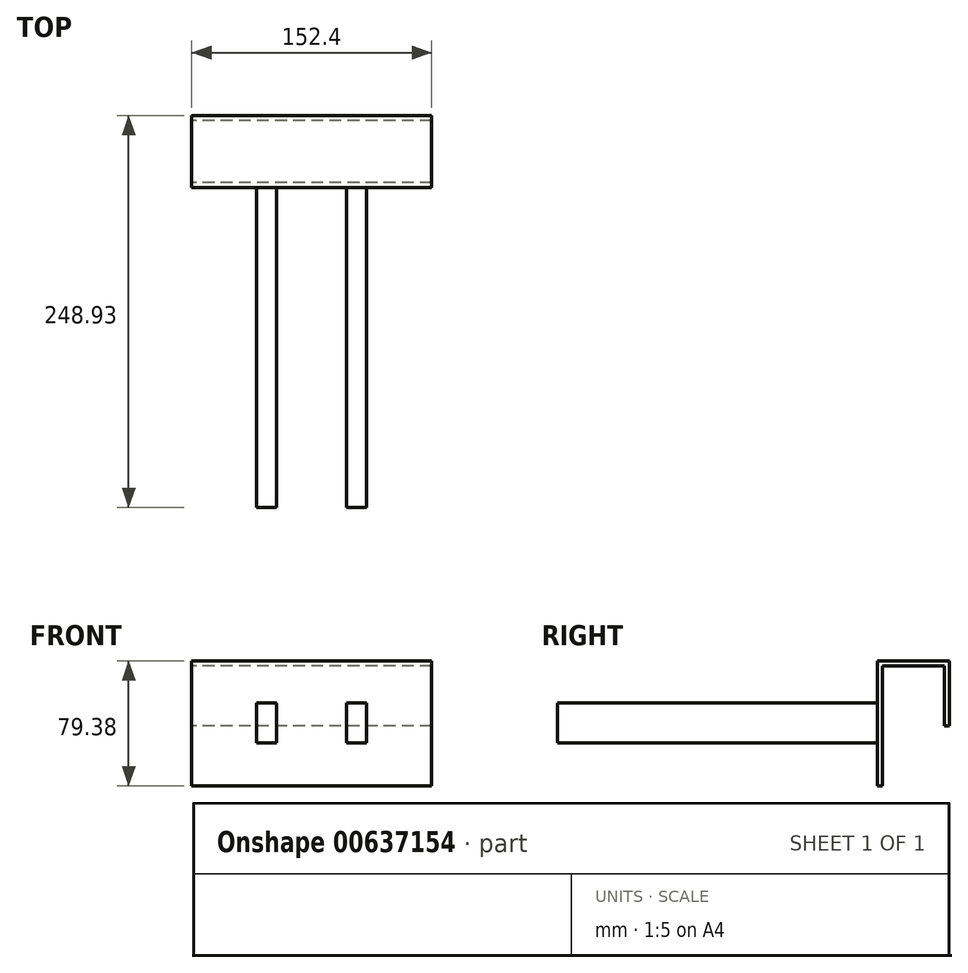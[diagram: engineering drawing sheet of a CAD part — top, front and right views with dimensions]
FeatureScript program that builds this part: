
annotation { "Feature Type Name" : "Feature", "Feature Type Description" : "" }
export const myFeature = defineFeature(function(context is Context, id is Id, definition is map)
    precondition{}
    {
        {
            var Q0;
            Q0=qCreatedBy(makeId("Right.planeOp"),FACE);
            var sketch = newSketch(context, id + "F0", { "sketchPlane" : qUnion([Q0])});
            skLineSegment(sketch, "E0", {"start": v(0, -76.2) * mm, "end": v(0, 0) * mm});
            skLineSegment(sketch, "E1", {"start": v(0, 0) * mm, "end": v(39.37, 0) * mm});
            skLineSegment(sketch, "E2", {"start": v(39.37, 0) * mm, "end": v(39.37, -38.1) * mm});
            skLineSegment(sketch, "E3.0", {"start": v(42.55, 3.18) * mm, "end": v(42.55, -38.1) * mm});
            skLineSegment(sketch, "E3.1", {"start": v(-3.17, 3.17) * mm, "end": v(42.55, 3.18) * mm});
            skLineSegment(sketch, "E3.2", {"start": v(-3.17, -76.2) * mm, "end": v(-3.17, 3.17) * mm});
            skLineSegment(sketch, "E4", {"start": v(-3.17, -76.2) * mm, "end": v(0, -76.2) * mm});
            skLineSegment(sketch, "E5", {"start": v(39.37, -38.1) * mm, "end": v(42.55, -38.1) * mm});
            skSolve(sketch);
        }
        {
            var Q0;
            Q0 = qSketchRegion(id + "F0", true);
            extrude(context, id + "F1", {"entities" : qUnion([Q0]), "depth" : 152.4 * mm, "offsetDistance" : 25.4 * mm});
        }
        {
            var Q0;
            Q0=makeQuery(id+"F1.opExtrude","SWEPT_FACE",FACE,{"disambiguationData":[OSD([sQuery(id+"F0.wireOp",EDGE,"E3.2")])]});
            var sketch = newSketch(context, id + "F2", { "sketchPlane" : qUnion([Q0])});
            skLineSegment(sketch, "E6.bottom", {"start": v(41.28, -23.35) * mm, "end": v(53.98, -23.35) * mm});
            skLineSegment(sketch, "E6.top", {"start": v(41.28, -48.75) * mm, "end": v(53.98, -48.75) * mm});
            skLineSegment(sketch, "E6.left", {"start": v(41.28, -23.35) * mm, "end": v(41.28, -48.75) * mm});
            skLineSegment(sketch, "E6.right", {"start": v(53.98, -23.35) * mm, "end": v(53.98, -48.75) * mm});
            skLineSegment(sketch, "E7.bottom", {"start": v(98.43, -23.35) * mm, "end": v(111.13, -23.35) * mm});
            skLineSegment(sketch, "E7.top", {"start": v(98.43, -48.75) * mm, "end": v(111.13, -48.75) * mm});
            skLineSegment(sketch, "E7.left", {"start": v(98.43, -23.35) * mm, "end": v(98.43, -48.75) * mm});
            skLineSegment(sketch, "E7.right", {"start": v(111.13, -23.35) * mm, "end": v(111.13, -48.75) * mm});
            skLineSegment(sketch, "E8", {"start": v(76.2, 3.17) * mm, "end": v(76.2, -76.2) * mm, "construction": true});
            skSolve(sketch);
        }
        {
            var Q0;
            Q0 = qSketchRegion(id + "F2", true);
            extrude(context, id + "F3", {"entities" : qUnion([Q0]), "operationType" : NewBodyOperationType.ADD, "depth" : 203.2 * mm, "offsetDistance" : 25.4 * mm});
        }
    });
